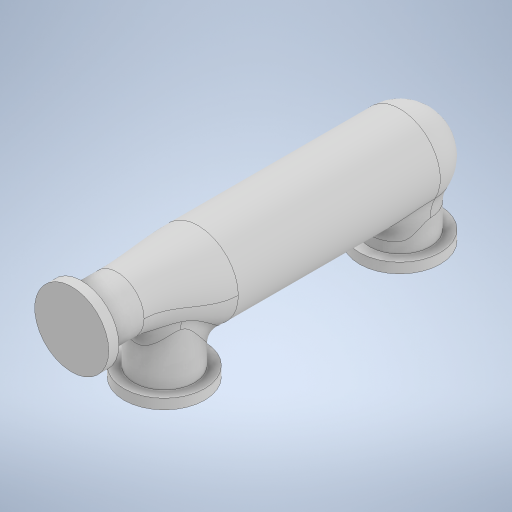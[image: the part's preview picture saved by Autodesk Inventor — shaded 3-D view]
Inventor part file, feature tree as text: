
AUTODESK INVENTOR PART (.ipt)
format: ipt  version: 2023 (Build 270158000, 158)  size: 446,464 bytes
history: native  units: in
note: dims shown in document units (in); Inventor stores cm internally (conversion verified against a paired STEP export)
features: sketch x6, extrude x5, other x2, fillet x2, revolve x1, plane x1, loft x1, projected_geometry x1
ambient origin geometry x8: Origin, YZ Plane, XZ Plane, XY Plane, X Axis, Y Axis, Z Axis, Center Point
bodies: Solid1 (feature_tree)
feature tree (19):
  other  "intake_manifold_r"
  revolve  "Revolution1"  [1 undecoded]
  plane  "Work Plane1"
  loft  "Loft1"
  extrude  "Extrusion1"  Depth=0.3937in
  fillet  "Fillet1"  Radius=0.3937in
  extrude  "Extrusion2"  Depth=0.3937in
  extrude  "Extrusion3"  Depth=11.0in TaperAngle=0.0deg
  extrude  "Extrusion5"  Depth=1.5in
  fillet  "Fillet3"  Radius=1.5in
  extrude  "Extrusion6"  Depth=1.5in
  sketch  "Sketch3"  dims[d3=30.0in d4=6.0in]
  other  "Edges1"
  sketch  "Sketch4"  dims[d5=90.0deg d6=12.0in]
  sketch  "Sketch5"  dims[d7=8.0in d8=2.0in d9=0.3937in d10=90.0deg]
  projected_geometry  "Projected Loop1"
  sketch  "Sketch6"  dims[d13=0.3937in d14=90.0deg d15=9.0in]
  sketch  "Sketch8"  dims[d16=9.0in d17=11.0in d18=0.0in]
  sketch  "Sketch9"  dims[d20=12.0in d21=12.0in d22=1.5in d23=0.0in d24=6.0in d25=6.0in d26=6.0in d27=0.0in d28=2.0in d29=0.1969in d30=6.0in d31=0.3937in d33=1.0in d34=0.0in d48=2.5in d49=5.0in d50=5.25in d51=0.0in d52=3.0in d53=3.0in d54=3.0in d55=0.0in d56=3.0in d57=0.1969in d58=2.0in d59=0.2953in d60=2.0in d61=0.0984in d62=11.0in d63=1.5in d64=0.0in d65=0.5in d66=0.0344in d67=0.5in d68=0.0344in]
note: 1 required parameter value undecoded (feature->parameter linkage not recoverable at this tier; creation-order binding heuristic only, values carry confidence <= 0.55)
